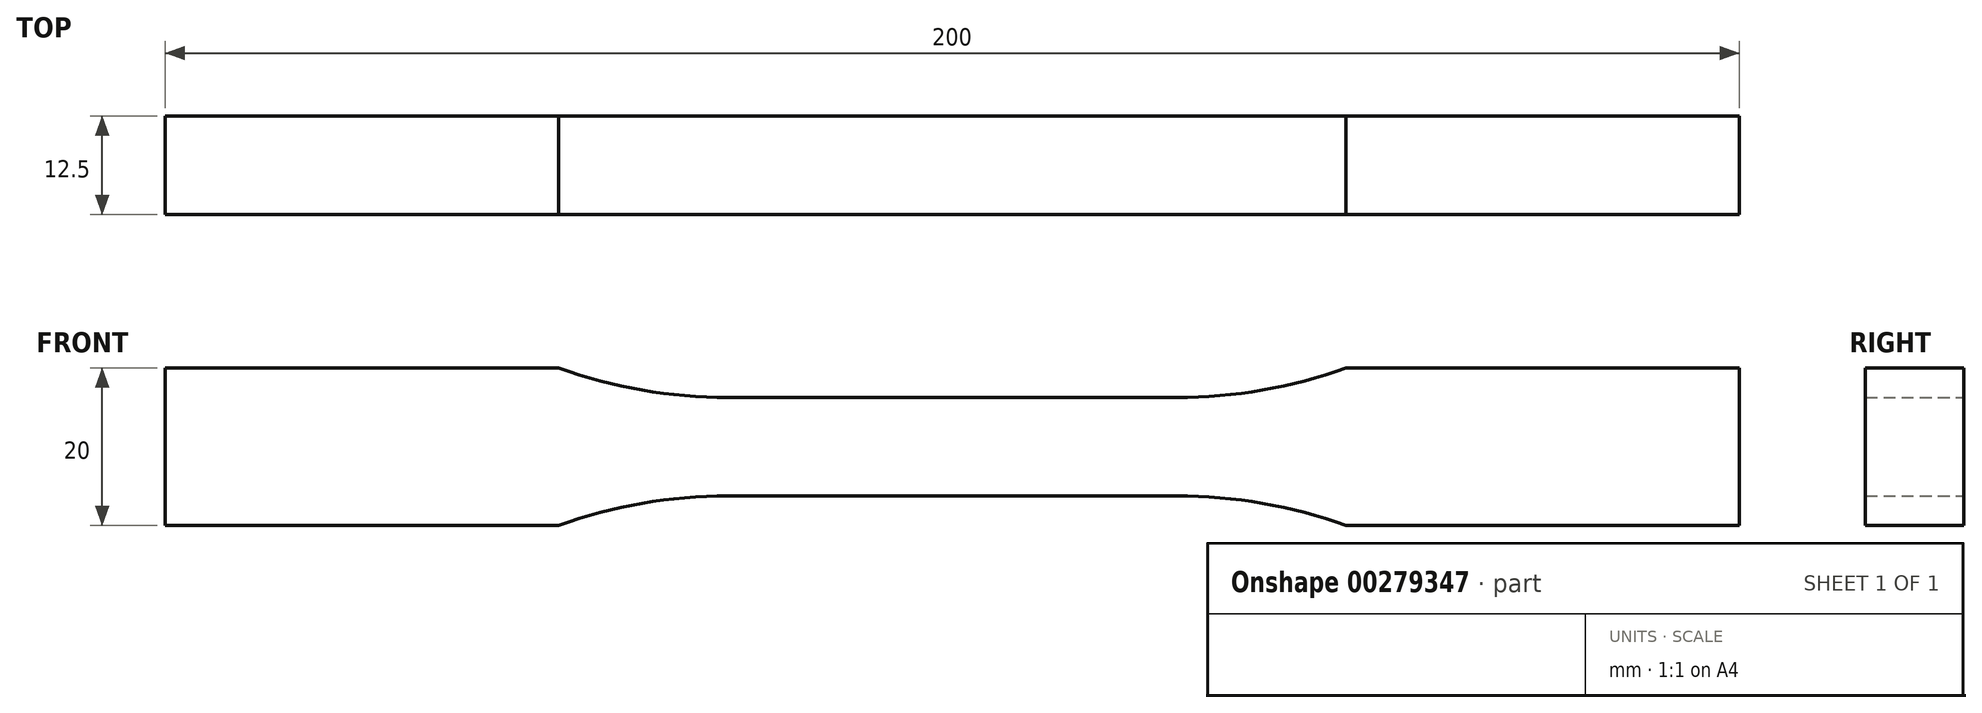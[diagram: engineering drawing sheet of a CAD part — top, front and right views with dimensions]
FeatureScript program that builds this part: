
annotation { "Feature Type Name" : "Feature", "Feature Type Description" : "" }
export const myFeature = defineFeature(function(context is Context, id is Id, definition is map)
    precondition{}
    {
        {
            var Q0;
            Q0=qCreatedBy(makeId("Front.planeOp"),FACE);
            var sketch = newSketch(context, id + "F0", { "sketchPlane" : qUnion([Q0])});
            skLineSegment(sketch, "E0", {"start": v(0, 6.25) * mm, "end": v(28.5, 6.25) * mm});
            skArc(sketch, "E1", {"start": v(28.5, 6.25) * mm, "mid": v(39.41, 7.2) * mm, "end": v(50, 10) * mm});
            skLineSegment(sketch, "E2", {"start": v(50, 10) * mm, "end": v(100, 10) * mm});
            skLineSegment(sketch, "E3", {"start": v(100, 10) * mm, "end": v(100, 0) * mm});
            skLineSegment(sketch, "E4.MirrorCS", {"start": v(0, -6.25) * mm, "end": v(28.5, -6.25) * mm});
            skLineSegment(sketch, "E5.MirrorCS", {"start": v(100, -10) * mm, "end": v(100, 0) * mm});
            skLineSegment(sketch, "E6.MirrorCS", {"start": v(50, -10) * mm, "end": v(100, -10) * mm});
            skArc(sketch, "E7.MirrorCS", {"start": v(28.5, -6.25) * mm, "mid": v(39.41, -7.2) * mm, "end": v(50, -10) * mm});
            skArc(sketch, "E8.MirrorCS", {"start": v(-28.5, -6.25) * mm, "mid": v(-39.41, -7.2) * mm, "end": v(-50, -10) * mm});
            skLineSegment(sketch, "E9.MirrorCS", {"start": v(-50, -10) * mm, "end": v(-100, -10) * mm});
            skArc(sketch, "E10.MirrorCS", {"start": v(-28.5, 6.25) * mm, "mid": v(-39.41, 7.2) * mm, "end": v(-50, 10) * mm});
            skLineSegment(sketch, "E11.MirrorCS", {"start": v(-50, 10) * mm, "end": v(-100, 10) * mm});
            skLineSegment(sketch, "E12.MirrorCS", {"start": v(-100, -10) * mm, "end": v(-100, 0) * mm});
            skLineSegment(sketch, "E13.MirrorCS", {"start": v(0, -6.25) * mm, "end": v(-28.5, -6.25) * mm});
            skLineSegment(sketch, "E14.MirrorCS", {"start": v(-100, 10) * mm, "end": v(-100, 0) * mm});
            skLineSegment(sketch, "E15.MirrorCS", {"start": v(0, 6.25) * mm, "end": v(-28.5, 6.25) * mm});
            skSolve(sketch);
        }
        {
            var Q0;
            Q0=makeQuery(id+"F0.imprint","IMPRINT",FACE,{"disambiguationData":[TD([[makeQuery(id+"F0.imprint","IMPRINT",EDGE,{"derivedFrom":sQuery(id+"F0.wireOp",EDGE,"E0")}),-1.0]])]});
            extrude(context, id + "F1", {"entities" : qUnion([Q0]), "depth" : 12.5 * mm});
        }
    });
